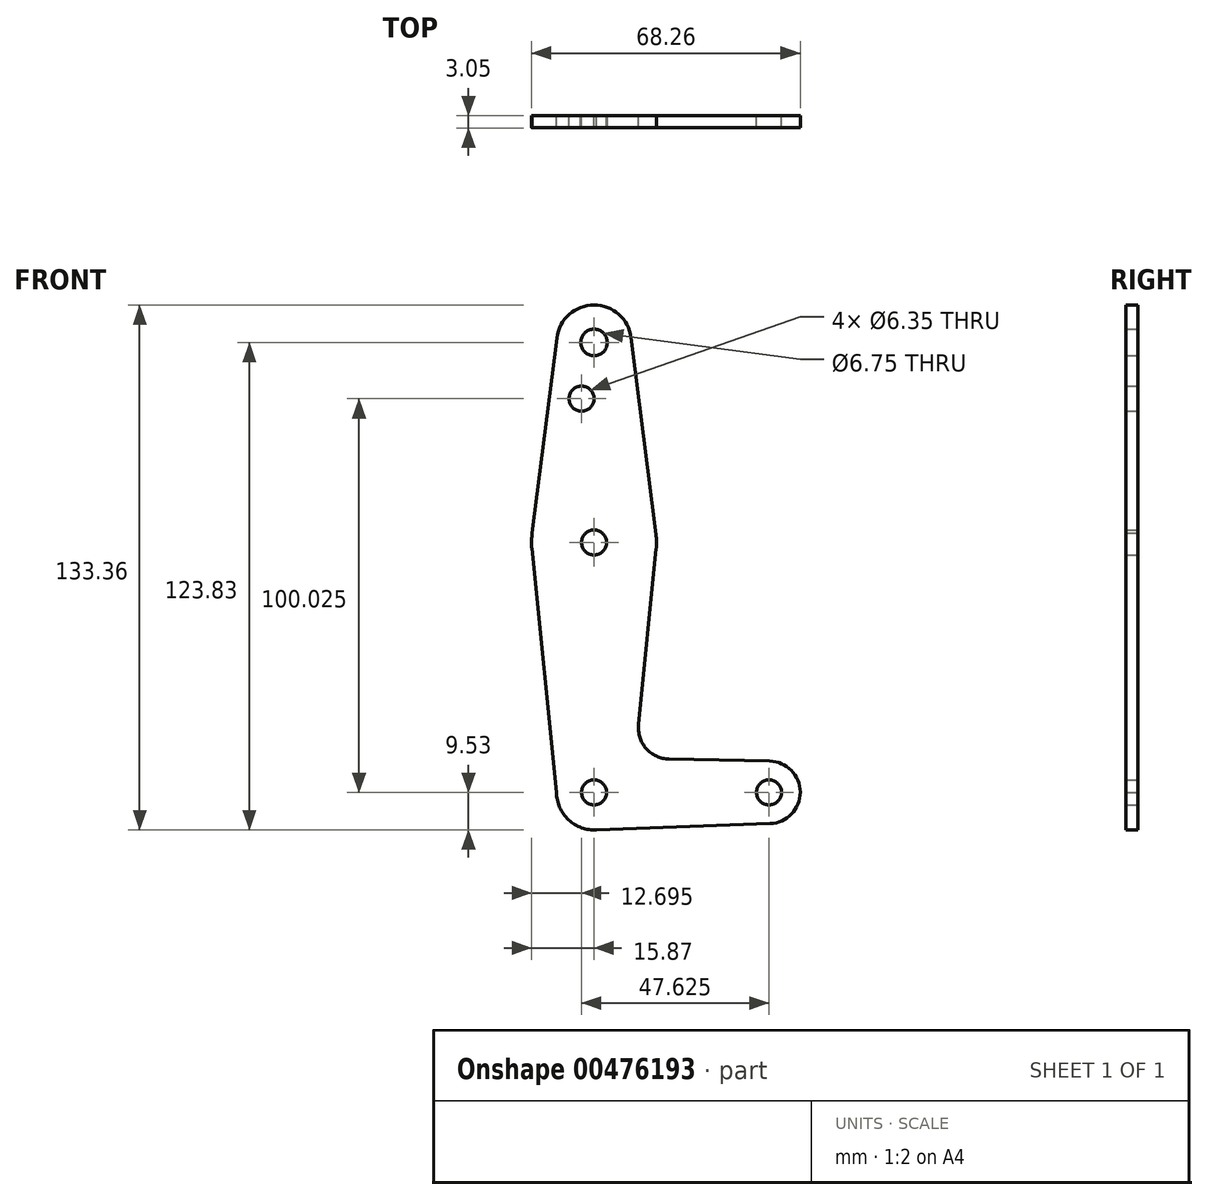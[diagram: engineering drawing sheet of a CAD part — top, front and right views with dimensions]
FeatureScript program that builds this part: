
annotation { "Feature Type Name" : "Feature", "Feature Type Description" : "" }
export const myFeature = defineFeature(function(context is Context, id is Id, definition is map)
    precondition{}
    {
        {
            var Q0;
            Q0=qCreatedBy(makeId("Front.planeOp"),FACE);
            var sketch = newSketch(context, id + "F0", { "sketchPlane" : qUnion([Q0])});
            skLineSegment(sketch, "E0", {"start": v(0, 0) * mm, "end": v(44.45, 0) * mm, "construction": true});
            skLineSegment(sketch, "E1", {"start": v(0, 0) * mm, "end": v(0, 114.3) * mm, "construction": true});
            skCircle(sketch, "E2", {"center": v(0, 114.3) * mm, "radius": 9.53 * mm});
            skCircle(sketch, "E3", {"center": v(0, 0) * mm, "radius": 9.53 * mm});
            skCircle(sketch, "E4", {"center": v(0, 63.5) * mm, "radius": 15.88 * mm});
            skCircle(sketch, "E5", {"center": v(44.45, 0) * mm, "radius": 7.94 * mm});
            skLineSegment(sketch, "E6", {"start": v(-9.53, 0) * mm, "end": v(-15.8, 61.9) * mm});
            skLineSegment(sketch, "E7", {"start": v(-15.8, 65.1) * mm, "end": v(-9.45, 115.49) * mm});
            skLineSegment(sketch, "E8", {"start": v(15.8, 61.9) * mm, "end": v(11.3, 17.2) * mm});
            skLineSegment(sketch, "E9", {"start": v(9.45, 115.5) * mm, "end": v(15.75, 65.48) * mm});
            skLineSegment(sketch, "E10", {"start": v(19.05, 8.46) * mm, "end": v(44.61, 7.94) * mm});
            skLineSegment(sketch, "E11", {"start": v(0, -9.52) * mm, "end": v(44.73, -7.93) * mm});
            skPoint(sketch, "E12.newPointA", {"position": v(9.57, 0) * mm});
            skArc(sketch, "E12.filletArc", {"start": v(11.3, 17.2) * mm, "mid": v(13.26, 11.14) * mm, "end": v(19.05, 8.46) * mm});
            skCircle(sketch, "E13", {"center": v(0, 114.3) * mm, "radius": 3.38 * mm});
            skCircle(sketch, "E14", {"center": v(0, 114.3) * mm, "radius": 3.18 * mm});
            skCircle(sketch, "E15", {"center": v(0, 63.5) * mm, "radius": 3.18 * mm});
            skCircle(sketch, "E16", {"center": v(0, 0) * mm, "radius": 3.18 * mm});
            skCircle(sketch, "E17", {"center": v(44.45, 0) * mm, "radius": 3.18 * mm});
            skCircle(sketch, "E18", {"center": v(-3.18, 100.03) * mm, "radius": 3.18 * mm});
            skSolve(sketch);
        }
        {
            var Q0;
            Q0 = qSketchRegion(id + "F0", true);
            extrude(context, id + "F1", {"entities" : qUnion([Q0]), "depth" : 3.05 * mm});
        }
    });
